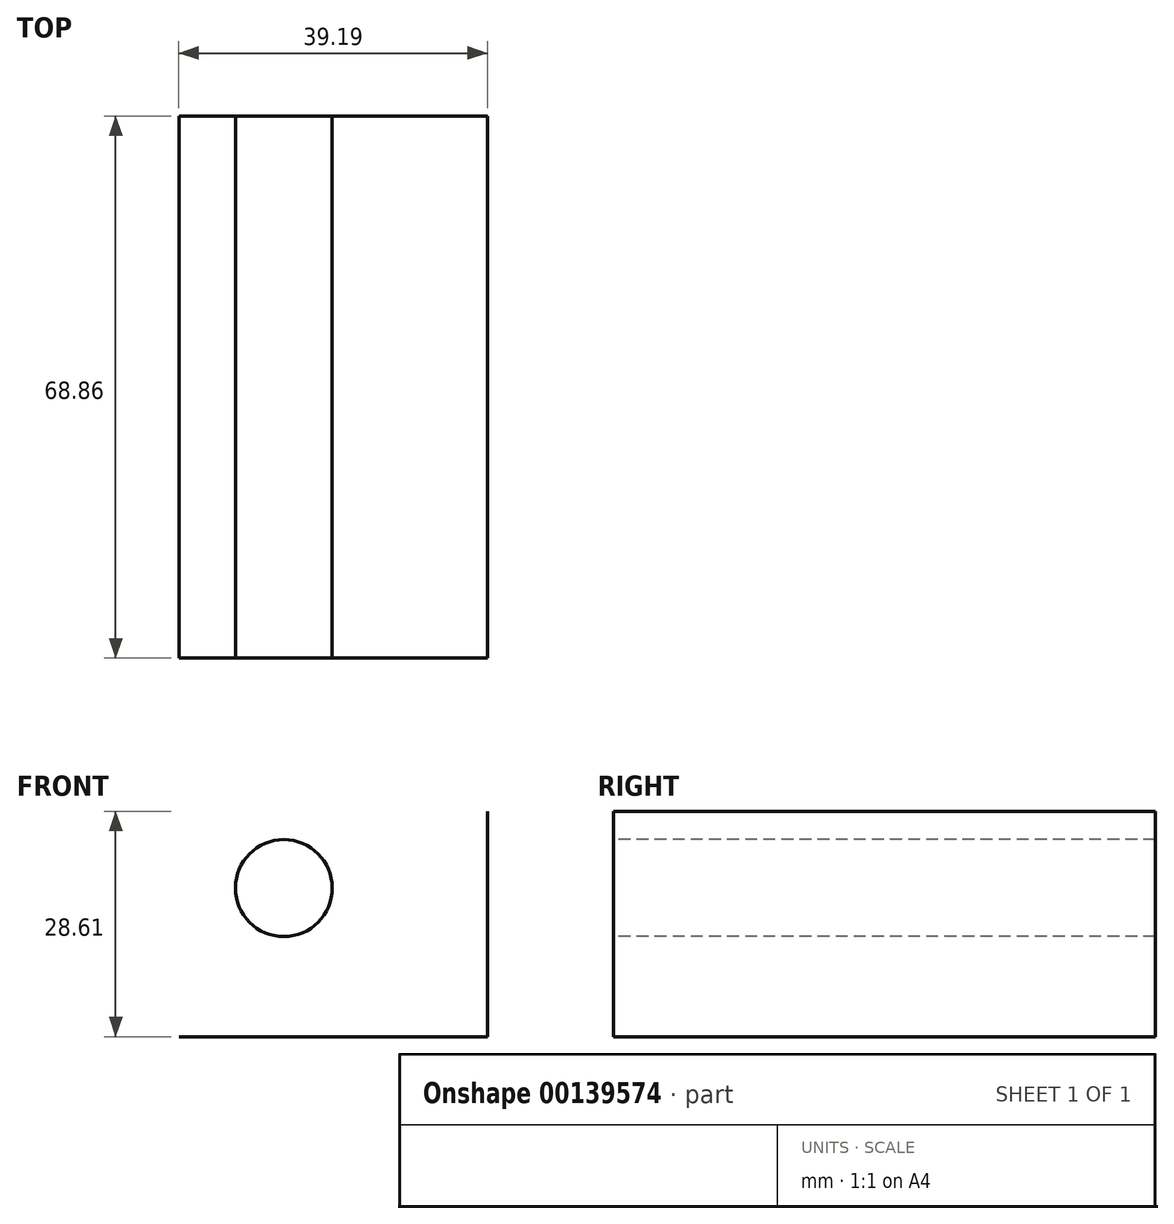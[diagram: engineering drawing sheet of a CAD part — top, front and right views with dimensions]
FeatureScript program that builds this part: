
annotation { "Feature Type Name" : "Feature", "Feature Type Description" : "" }
export const myFeature = defineFeature(function(context is Context, id is Id, definition is map)
    precondition{}
    {
        {
            var Q0;
            Q0=qCreatedBy(makeId("Front.planeOp"),FACE);
            var sketch = newSketch(context, id + "F0", { "sketchPlane" : qUnion([Q0])});
            skLineSegment(sketch, "E0", {"start": v(-50.24, 34.35) * mm, "end": v(-89.45, 34.35) * mm});
            skLineSegment(sketch, "E1", {"start": v(-89.45, 34.35) * mm, "end": v(-89.45, 5.74) * mm});
            skLineSegment(sketch, "E2", {"start": v(-89.45, 5.74) * mm, "end": v(-50.26, 5.74) * mm});
            skLineSegment(sketch, "E3", {"start": v(-50.26, 5.74) * mm, "end": v(-50.26, 34.35) * mm});
            skCircle(sketch, "E4", {"center": v(-76.11, 24.62) * mm, "radius": 6.15 * mm});
            skSolve(sketch);
        }
        {
            var Q0;
            Q0=sQuery(id+"F0.wireOp",EDGE,"E4");
            var Q1;
            Q1=sQuery(id+"F0.wireOp",EDGE,"E3");
            var Q2;
            Q2=sQuery(id+"F0.wireOp",EDGE,"E2");
            extrude(context, id + "F1", {"bodyType" : ToolBodyType.SURFACE, "surfaceEntities" : qUnion([Q0, Q1, Q2]), "depth" : 68.86 * mm});
        }
    });
